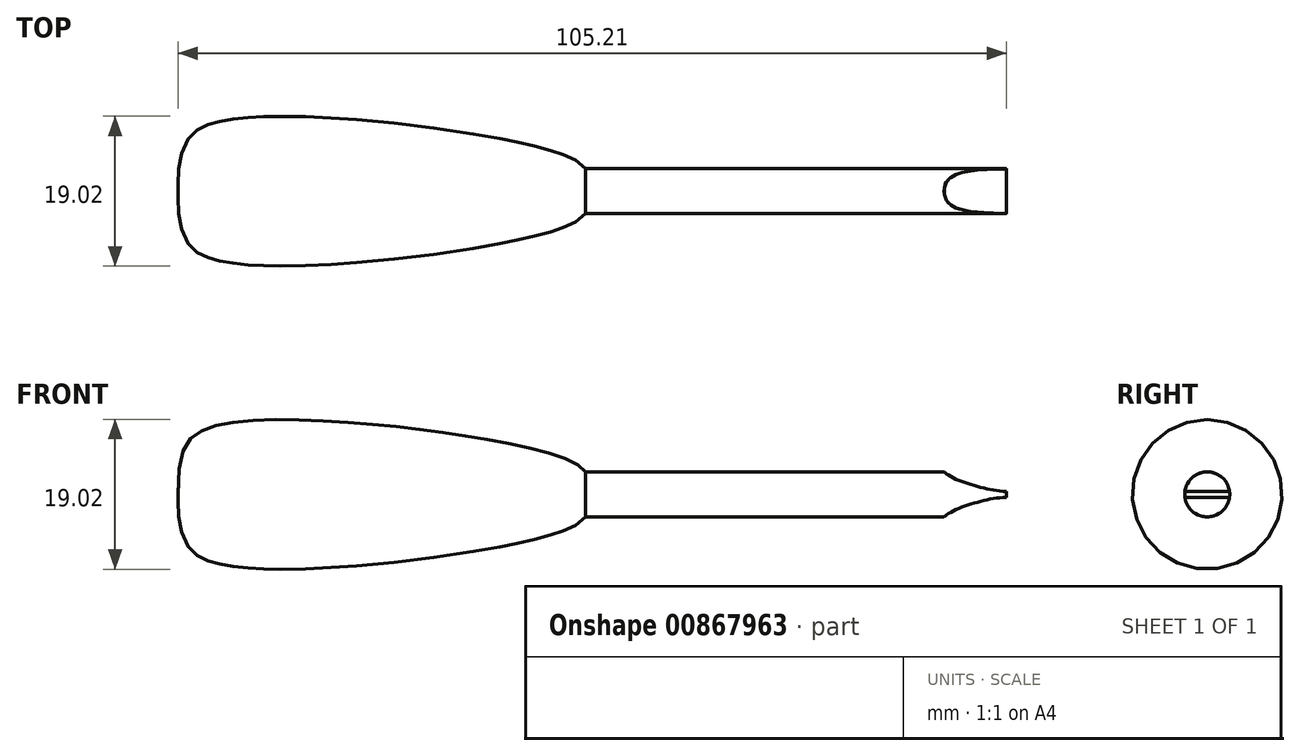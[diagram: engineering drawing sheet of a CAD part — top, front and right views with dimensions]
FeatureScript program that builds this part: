
annotation { "Feature Type Name" : "Feature", "Feature Type Description" : "" }
export const myFeature = defineFeature(function(context is Context, id is Id, definition is map)
    precondition{}
    {
        {
            var Q0;
            Q0=qCreatedBy(makeId("Front.planeOp"),FACE);
            var sketch = newSketch(context, id + "F0", { "sketchPlane" : qUnion([Q0])});
            skLineSegment(sketch, "E0", {"start": v(0, 0) * mm, "end": v(-70.06, 0) * mm, "construction": true});
            skLineSegment(sketch, "E1", {"start": v(-70.06, 0) * mm, "end": v(64.3, 0) * mm, "construction": true});
            skLineSegment(sketch, "E2", {"start": v(0, 0) * mm, "end": v(0, 56.63) * mm});
            skFitSpline(sketch, "E3", {"points": [v(-51.77, 0) * mm, v(-47.48, 8.58) * mm, v(-29.38, 9.09) * mm, v(-9.47, 6.37) * mm, v(0, 2.86) * mm], "startDerivative": vector(-2.11, 86.86) * mm, "endDerivative": vector(14.3, -22.06) * mm});
            skLineSegment(sketch, "E4", {"start": v(0, 2.86) * mm, "end": v(0, 2.86) * mm});
            skLineSegment(sketch, "E5", {"start": v(0, 2.86) * mm, "end": v(53.43, 2.86) * mm});
            skLineSegment(sketch, "E6", {"start": v(53.43, 2.86) * mm, "end": v(53.43, 0) * mm});
            skLineSegment(sketch, "E7", {"start": v(53.43, 0) * mm, "end": v(-51.77, 0) * mm});
            skSolve(sketch);
        }
        {
            var Q0;
            {var subQ4=sQuery(id+"F0.wireOp",EDGE,"E3");Q0=makeQuery(id+"F0.imprint","IMPRINT",FACE,{"disambiguationData":[TD([[makeQuery(id+"F0.imprint","IMPRINT",EDGE,{"derivedFrom":subQ4}),-1.0]])]});}
            var Q1;
            {var subQ3=sQuery(id+"F0.wireOp",EDGE,"E5");Q1=makeQuery(id+"F0.imprint","IMPRINT",FACE,{"disambiguationData":[TD([[makeQuery(id+"F0.imprint","IMPRINT",EDGE,{"derivedFrom":subQ3}),-1.0]])]});}
            var Q2;
            Q2=sQuery(id+"F0.wireOp",EDGE,"E7");
            revolve(context, id + "F1", {"surfaceOperationType" : NewSurfaceOperationType.NEW, "entities" : qUnion([Q0, Q1]), "axis" : qUnion([Q2]), "revolveType" : RevolveType.FULL});
        }
        {
            var Q0;
            Q0=qCreatedBy(makeId("Front.planeOp"),FACE);
            var sketch = newSketch(context, id + "F2", { "sketchPlane" : qUnion([Q0])});
            skFitSpline(sketch, "E8", {"points": [v(45.25, 3.14) * mm, v(49.2, 1.15) * mm, v(56.13, 0.58) * mm], "startDerivative": vector(4.42, -5.64) * mm, "endDerivative": vector(12.8, 2.87) * mm});
            skFitSpline(sketch, "E9.MirrorCS", {"points": [v(45.25, -3.14) * mm, v(49.2, -1.15) * mm, v(56.13, -0.58) * mm], "startDerivative": vector(4.42, 5.64) * mm, "endDerivative": vector(12.8, -2.87) * mm});
            skLineSegment(sketch, "E10", {"start": v(45.25, 3.14) * mm, "end": v(55.85, 3.14) * mm});
            skLineSegment(sketch, "E11", {"start": v(55.85, 3.14) * mm, "end": v(56.13, 0.58) * mm});
            skLineSegment(sketch, "E12", {"start": v(45.25, -3.14) * mm, "end": v(55.83, -3.5) * mm});
            skLineSegment(sketch, "E13", {"start": v(55.83, -3.5) * mm, "end": v(56.13, -0.58) * mm});
            skSolve(sketch);
        }
        {
            var Q0;
            Q0 = qSketchRegion(id + "F2", true);
            extrude(context, id + "F3", {"entities" : qUnion([Q0]), "operationType" : NewBodyOperationType.REMOVE, "oppositeDirection" : true, "depth" : 25 * mm, "offsetDistance" : 25 * mm, "hasSecondDirection" : true, "secondDirectionOppositeDirection" : false, "secondDirectionDepth" : 25 * mm});
        }
    });
